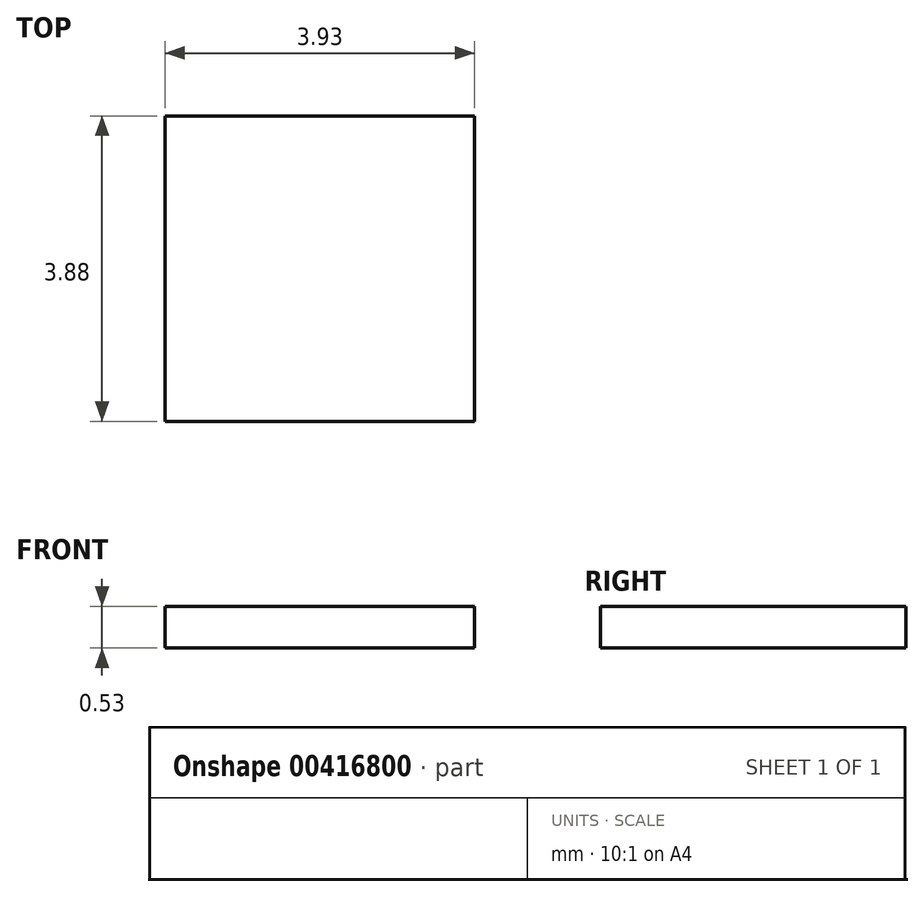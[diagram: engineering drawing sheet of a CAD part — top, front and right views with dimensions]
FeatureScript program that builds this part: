
annotation { "Feature Type Name" : "Feature", "Feature Type Description" : "" }
export const myFeature = defineFeature(function(context is Context, id is Id, definition is map)
    precondition{}
    {
        {
            var Q0;
            Q0=qCreatedBy(makeId("Top.planeOp"),FACE);
            var sketch = newSketch(context, id + "F0", { "sketchPlane" : qUnion([Q0])});
            skLineSegment(sketch, "E0.bottom", {"start": v(0, 0) * mm, "end": v(3.93, 0) * mm});
            skLineSegment(sketch, "E0.top", {"start": v(0, 3.88) * mm, "end": v(3.93, 3.88) * mm});
            skLineSegment(sketch, "E0.left", {"start": v(0, 0) * mm, "end": v(0, 3.88) * mm});
            skLineSegment(sketch, "E0.right", {"start": v(3.93, 0) * mm, "end": v(3.93, 3.88) * mm});
            skSolve(sketch);
        }
        {
            var Q0;
            Q0 = qSketchRegion(id + "F0", true);
            extrude(context, id + "F1", {"entities" : qUnion([Q0]), "depth" : .53 * mm, "offsetDistance" : 25.4 * mm});
        }
    });
